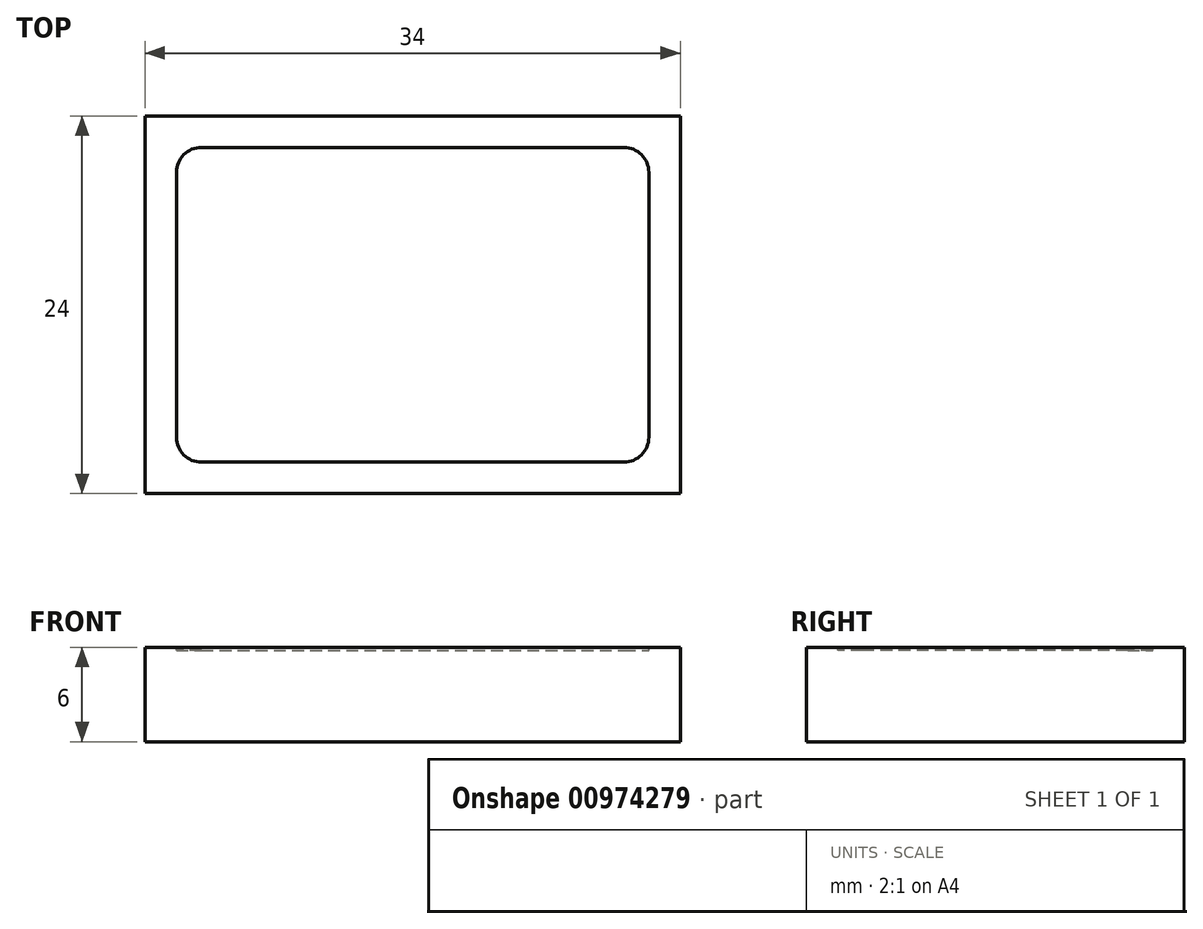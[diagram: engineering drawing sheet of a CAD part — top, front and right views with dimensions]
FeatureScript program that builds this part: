
annotation { "Feature Type Name" : "Feature", "Feature Type Description" : "" }
export const myFeature = defineFeature(function(context is Context, id is Id, definition is map)
    precondition{}
    {
        {
            var Q0;
            Q0=qCreatedBy(makeId("Top.planeOp"),FACE);
            var sketch = newSketch(context, id + "F0", { "sketchPlane" : qUnion([Q0])});
            skLineSegment(sketch, "E0.bottom", {"start": v(0, 0) * mm, "end": v(30, 0) * mm});
            skLineSegment(sketch, "E0.top", {"start": v(0, -20) * mm, "end": v(30, -20) * mm});
            skLineSegment(sketch, "E0.left", {"start": v(0, 0) * mm, "end": v(0, -20) * mm});
            skLineSegment(sketch, "E0.right", {"start": v(30, 0) * mm, "end": v(30, -20) * mm});
            skLineSegment(sketch, "E1.bottom", {"start": v(-2, 2) * mm, "end": v(32, 2) * mm});
            skLineSegment(sketch, "E1.top", {"start": v(-2, -22) * mm, "end": v(32, -22) * mm});
            skLineSegment(sketch, "E1.left", {"start": v(-2, 2) * mm, "end": v(-2, -22) * mm});
            skLineSegment(sketch, "E1.right", {"start": v(32, 2) * mm, "end": v(32, -22) * mm});
            skLineSegment(sketch, "E2", {"start": v(15, 2) * mm, "end": v(15, -22) * mm, "construction": true});
            skLineSegment(sketch, "E3", {"start": v(-2, -10) * mm, "end": v(32, -10) * mm, "construction": true});
            skPoint(sketch, "E4", {"position": v(15, 0) * mm});
            skPoint(sketch, "E5", {"position": v(30, -10) * mm});
            skSolve(sketch);
        }
        {
            var Q0;
            Q0=makeQuery(id+"F0.imprint","IMPRINT",FACE,{"disambiguationData":[TD([[makeQuery(id+"F0.imprint","IMPRINT",EDGE,{"derivedFrom":sQuery(id+"F0.wireOp",EDGE,"E0.bottom")}),-1.0]])]});
            var Q1;
            Q1=makeQuery(id+"F0.imprint","IMPRINT",FACE,{"disambiguationData":[TD([[makeQuery(id+"F0.imprint","IMPRINT",EDGE,{"derivedFrom":sQuery(id+"F0.wireOp",EDGE,"E0.bottom")}),1.0]])]});
            extrude(context, id + "F1", {"entities" : qUnion([Q0, Q1]), "oppositeDirection" : true, "depth" : 6 * mm, "offsetDistance" : 25 * mm});
        }
        {
            var Q0;
            Q0=makeQuery(id+"F0.imprint","IMPRINT",FACE,{"disambiguationData":[TD([[makeQuery(id+"F0.imprint","IMPRINT",EDGE,{"derivedFrom":sQuery(id+"F0.wireOp",EDGE,"E0.bottom")}),-1.0]])]});
            extrude(context, id + "F2", {"entities" : qUnion([Q0]), "operationType" : NewBodyOperationType.REMOVE, "oppositeDirection" : true, "depth" : 0.2 * mm, "offsetDistance" : 25 * mm});
        }
        {
            var Q0;
            Q0=makeQuery(id+"F2.boolean.opBoolean","COPY",EDGE,{"derivedFrom":makeQuery(id+"F2.opExtrude","SWEPT_EDGE",EDGE,{"disambiguationData":[OSD([sQuery(id+"F0.wireOp",EDGE,"E0.bottom"),sQuery(id+"F0.wireOp",EDGE,"E0.left")])]})});
            var Q1;
            Q1=makeQuery(id+"F2.boolean.opBoolean","COPY",EDGE,{"derivedFrom":makeQuery(id+"F2.opExtrude","SWEPT_EDGE",EDGE,{"disambiguationData":[OSD([sQuery(id+"F0.wireOp",EDGE,"E0.bottom"),sQuery(id+"F0.wireOp",EDGE,"E0.right")])]})});
            var Q2;
            Q2=makeQuery(id+"F2.boolean.opBoolean","COPY",EDGE,{"derivedFrom":makeQuery(id+"F2.opExtrude","SWEPT_EDGE",EDGE,{"disambiguationData":[OSD([sQuery(id+"F0.wireOp",EDGE,"E0.top"),sQuery(id+"F0.wireOp",EDGE,"E0.right")])]})});
            var Q3;
            Q3=makeQuery(id+"F2.boolean.opBoolean","COPY",EDGE,{"derivedFrom":makeQuery(id+"F2.opExtrude","SWEPT_EDGE",EDGE,{"disambiguationData":[OSD([sQuery(id+"F0.wireOp",EDGE,"E0.top"),sQuery(id+"F0.wireOp",EDGE,"E0.left")])]})});
            fillet(context, id + "F3", {"entities" : qUnion([Q0, Q1, Q2, Q3]), "radius" : (3.17 / 2) * mm, "tangentPropagation" : true, "allowEdgeOverflow" : false});
        }
    });
